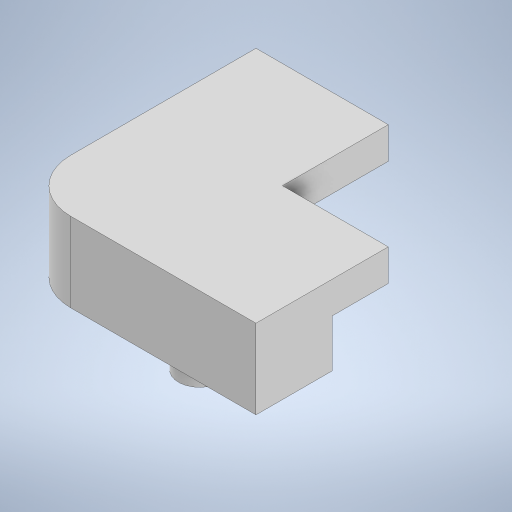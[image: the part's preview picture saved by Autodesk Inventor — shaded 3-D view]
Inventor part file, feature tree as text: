
AUTODESK INVENTOR PART (.ipt)
format: ipt  version: 2023.2 (Build 272271030, 271C)  size: 589,312 bytes
history: native  units: mm
features: extrude x5, sketch x5, projected_geometry x5, fillet x2
ambient origin geometry x8: Origin, YZ Plane, XZ Plane, XY Plane, X Axis, Y Axis, Z Axis, Center Point
bodies: Solid1 (feature_tree)
feature tree (17):
  extrude  "Extrusion1"  Depth=20.0mm
  extrude  "Extrusion2"  Depth=5.3mm TaperAngle=0.0deg
  extrude  "Extrusion3"  Depth=4.0mm
  extrude  "Extrusion4"  Depth=4.0mm TaperAngle=0.0deg
  fillet  "Fillet1"  Radius=2.0mm
  extrude  "Extrusion5"  Depth=5.0mm
  fillet  "Fillet2"  Radius=4.5mm
  sketch  "Sketch1"  dims[d3=20.0mm d4=20.0mm]
  sketch  "Sketch2"  dims[d5=7.5mm d6=0.0mm d7=5.3mm d8=0.0mm]
  projected_geometry  "Projected Loop1"
  projected_geometry  "Projected Loop2"
  sketch  "Sketch3"  dims[d9=5.3mm d10=0.0mm d11=4.0mm]
  projected_geometry  "Projected Loop3"
  sketch  "Sketch4"  dims[d12=4.0mm d13=4.0mm d14=0.0mm d15=2.0mm]
  projected_geometry  "Projected Loop4"
  sketch  "Sketch5"  dims[d16=9.67mm d17=9.67mm d18=4.5mm d19=25.0mm d20=25.0mm d21=7.5mm d22=0.0mm d23=5.0mm d24=0.5mm d25=0.872665mm d26=0.5mm d27=0.872665mm]
  projected_geometry  "Projected Loop5"
